# Revit family: Plumbing_Valves_TOTO-USA-Inc_EcoPower-Thermostatic-Mixing-Valve
name_source: partatom
category: Plumbing Fixtures
revit_build: Autodesk Revit 2015 (Build: 20140606_1530(x64)
units: mm (PartAtom-declared; Revit-internal decimal feet)

## types (1)
- TLT10R
    Ambient Temp. = 32 - 104°F (0 - 40°C)
    BIMobject category = Valves
    BIMobject category code = plumbing-valves
    BIMobject main category = Plumbing
    BIMobject main category code = plumbing
    Brand url = https://www.totousa.com
    Description = EcoPower Faucet Thermostatic Mixing Valve
    Edition number = 1
    Humidity = Max. 90% RH
    IFC Classification = Flow Terminal
    Manufacturer = TOTO USA
    Manufacturer name = TOTO USA Inc
    Masterformat 2014 Code = 10 28 00
    Masterformat 2014 Description = Toilet, Bath, and Laundry Accessories
    Material Plastic = Plastic - TOTO - White
    Material Steel = Metal - TOTO - Polished Steel
    Minimum Flow = 1 GPM
    Model = TLT10R
    OmniClass Code = 23-31 19 00
    OmniClass Description = Toilets
    Outlet Temp. = 100±4°F (38±2°C)
    Product Guid = 477223ad-e109-477f-b2dd-3a57d3631816
    Product SKU = toto-tlt10r
    Product certification = https://www.totousa.com
    Product data url = https://bimobject.com
    Product family = Valves
    Product group = Thermostatic Mixing
    Product name = EcoPower Thermostatic Mixing Valve
    Product url = https://www.totousa.com
    QR code = http://bimobject.com
    Recommended Temp.Range = Hot Supply: 120 - 180°F (49 -82°C),
Cold supply 39 - 80°F (4 - 27°C)
    Technical description = https://www.totousa.com
    UNSPSC Code = 30181505
    Uniclass 1.4 Code = L7216
    Uniclass 1.4 Description = Toilets
    Uniclass 2.0 Code = SS-35-65-90
    Uniclass 2.0 Description = Toilet Systems
    Uniclass 2015 Code = SL_35_80_89
    Uniclass 2015 Name = Toilets
    Uniformat II Code = D2030
    Uniformat II Description = Sanitary Waste
    Warranty = Three Years
    Water Supply Connection = 0' - 0 1/2"
    Water Supply Pressure(Max) = 80.00 psi
    Water Supply Pressure(Min) = 15.00 psi

## geometry (parser evidence)
native form markers: Sweep x3
no freeform markers — native parametric forms only
